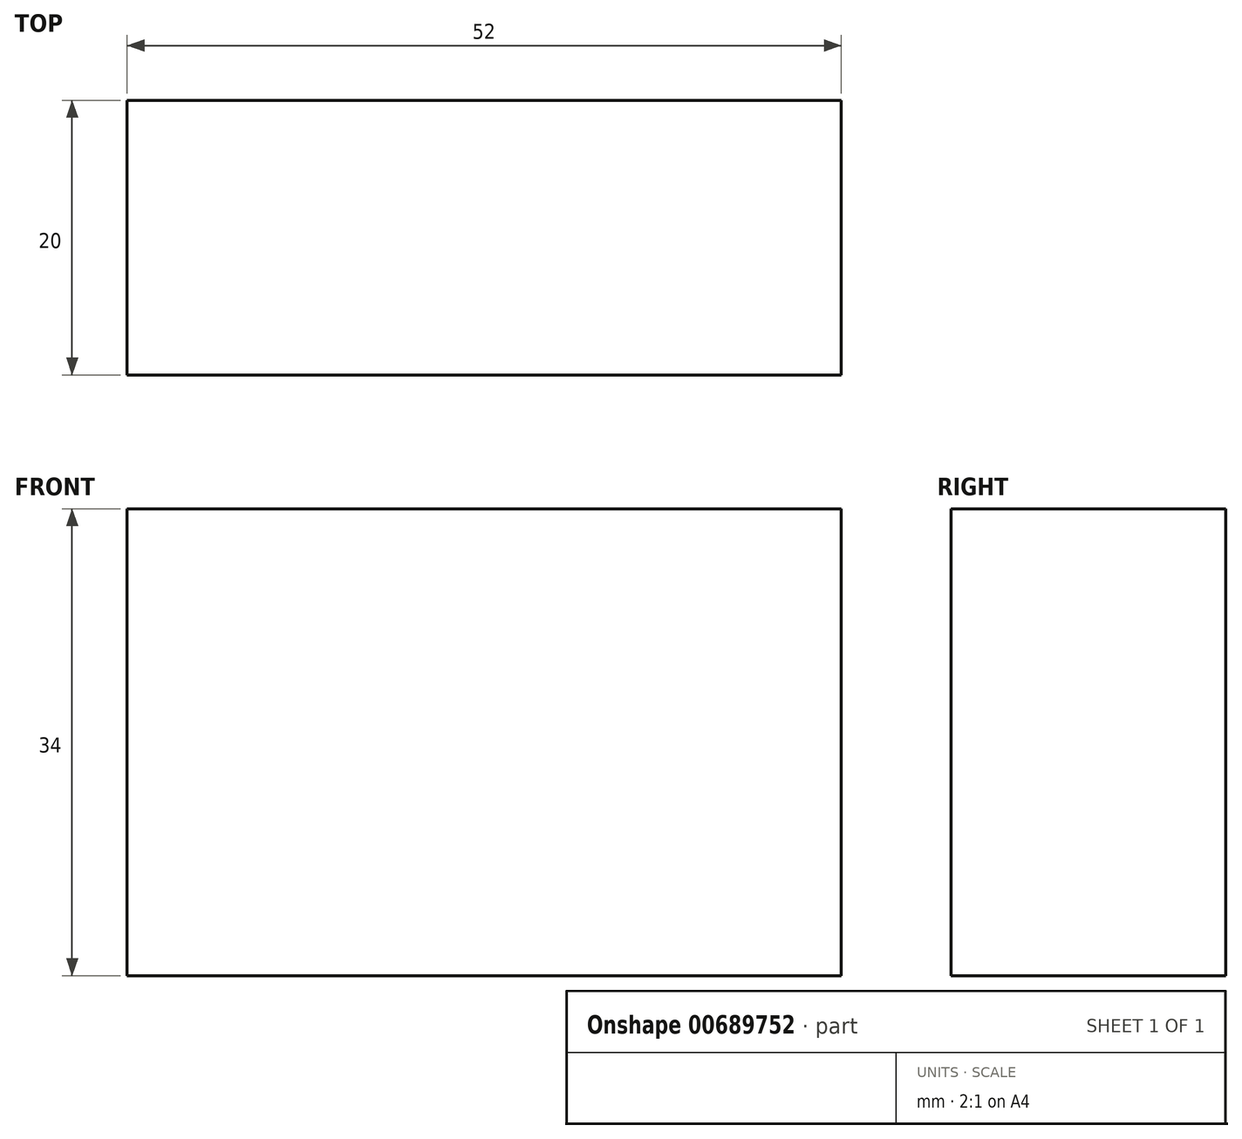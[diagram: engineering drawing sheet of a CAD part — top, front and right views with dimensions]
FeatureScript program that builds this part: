
annotation { "Feature Type Name" : "Feature", "Feature Type Description" : "" }
export const myFeature = defineFeature(function(context is Context, id is Id, definition is map)
    precondition{}
    {
        {
            var Q0;
            Q0=qCreatedBy(makeId("Front.planeOp"),FACE);
            var sketch = newSketch(context, id + "F0", { "sketchPlane" : qUnion([Q0])});
            skLineSegment(sketch, "E0.bottom", {"start": v(26, 17) * mm, "end": v(-26, 17) * mm});
            skLineSegment(sketch, "E0.top", {"start": v(26, -17) * mm, "end": v(-26, -17) * mm});
            skLineSegment(sketch, "E0.left", {"start": v(26, 17) * mm, "end": v(26, -17) * mm});
            skLineSegment(sketch, "E0.right", {"start": v(-26, 17) * mm, "end": v(-26, -17) * mm});
            skPoint(sketch, "E0.middle", {"position": v(0, 0) * mm});
            skSolve(sketch);
        }
        {
            var Q0;
            Q0=makeQuery(id+"F0.imprint","IMPRINT",FACE,{"disambiguationData":[TD([[makeQuery(id+"F0.imprint","IMPRINT",EDGE,{"derivedFrom":sQuery(id+"F0.wireOp",EDGE,"E0.bottom")}),1.0]])]});
            extrude(context, id + "F1", {"entities" : qUnion([Q0]), "depth" : 20 * mm, "offsetDistance" : 25.4 * mm});
        }
    });
